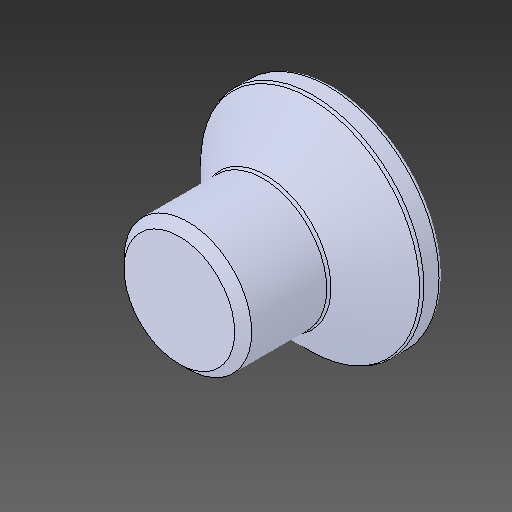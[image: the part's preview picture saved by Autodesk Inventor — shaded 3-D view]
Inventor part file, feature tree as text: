
AUTODESK INVENTOR PART (.ipt)
format: ipt  version: 2018.2 (Build 222227000, 227)  size: 138,752 bytes
history: native  units: mm
features: other x1, chamfer x1
ambient origin geometry x8: Origin, YZ Plane, XZ Plane, XY Plane, X Axis, Y Axis, Z Axis, Center Point
bodies: Body1 (feature_tree)
feature tree (2):
  other  "ソリッド1"
  chamfer  "Chamfer2"  [1 undecoded]
note: 1 required parameter value undecoded (feature->parameter linkage not recoverable at this tier; creation-order binding heuristic only, values carry confidence <= 0.55)
